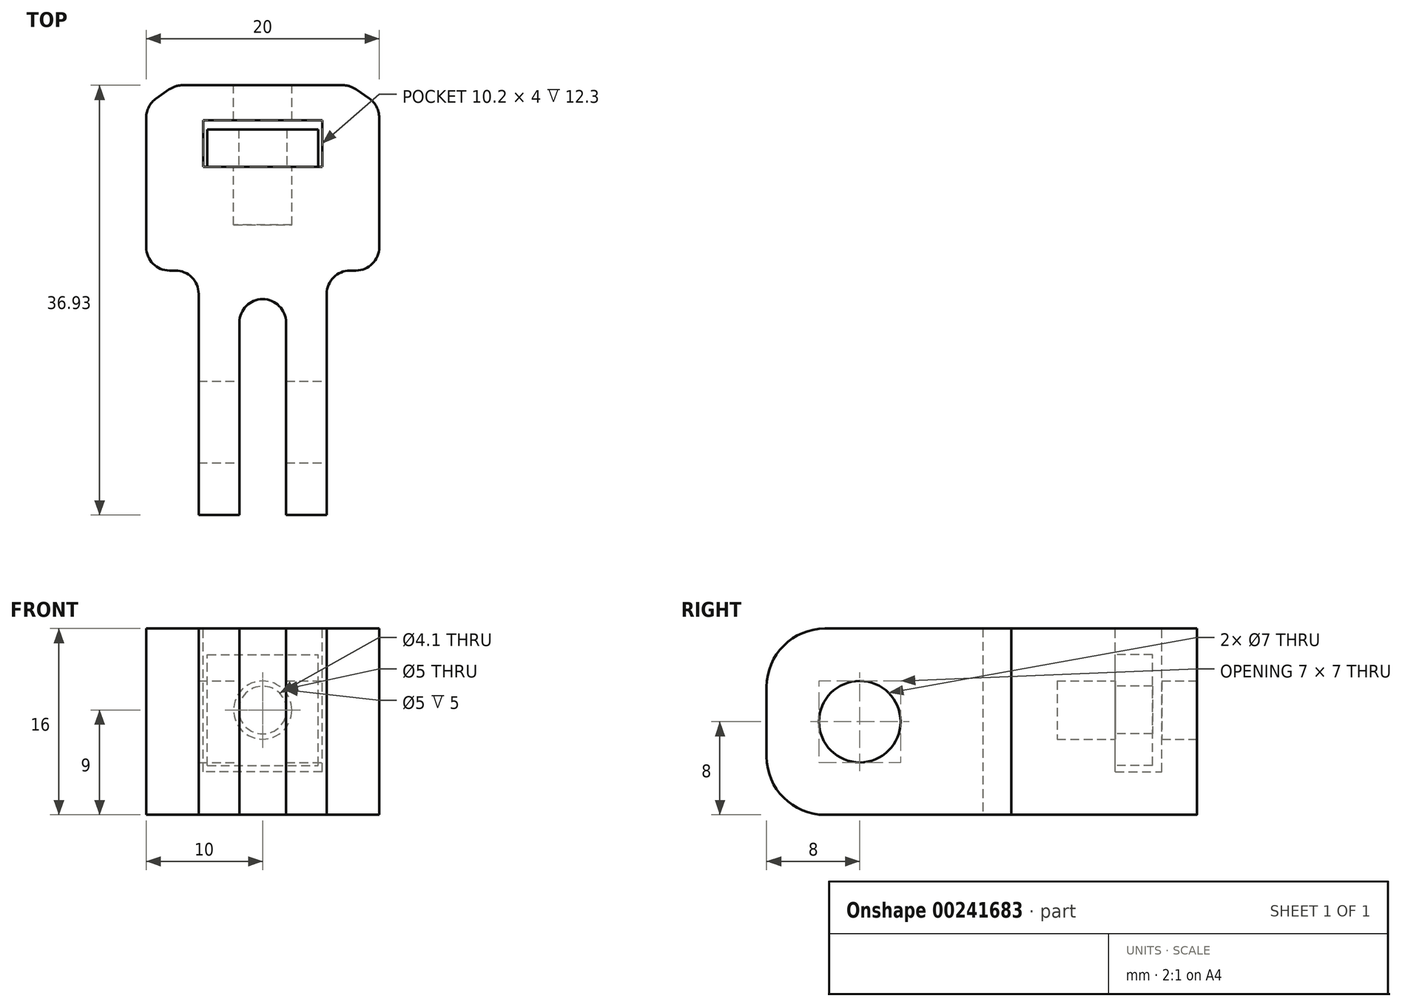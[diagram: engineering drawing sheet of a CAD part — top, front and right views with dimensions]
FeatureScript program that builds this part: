
annotation { "Feature Type Name" : "Feature", "Feature Type Description" : "" }
export const myFeature = defineFeature(function(context is Context, id is Id, definition is map)
    precondition{}
    {
        {
            var Q0;
            Q0=qCreatedBy(makeId("Top.planeOp"),FACE);
            var sketch = newSketch(context, id + "F0", { "sketchPlane" : qUnion([Q0])});
            skLineSegment(sketch, "E0.top", {"start": v(-5.5, -26) * mm, "end": v(-2, -26) * mm});
            skLineSegment(sketch, "E0.left", {"start": v(-5.5, -4.99) * mm, "end": v(-5.5, -26) * mm});
            skLineSegment(sketch, "E0.right", {"start": v(5.5, -4.99) * mm, "end": v(5.5, -26) * mm});
            skLineSegment(sketch, "E1.top", {"start": v(-2, -7.45) * mm, "end": v(2, -7.45) * mm});
            skLineSegment(sketch, "E1.left", {"start": v(-2, -26) * mm, "end": v(-2, -7.45) * mm});
            skLineSegment(sketch, "E1.right", {"start": v(2, -26) * mm, "end": v(2, -7.45) * mm});
            skLineSegment(sketch, "E2.trimOffspring", {"start": v(2, -26) * mm, "end": v(5.5, -26) * mm});
            skLineSegment(sketch, "E3.top", {"start": v(-7.5, 10.93) * mm, "end": v(7.5, 10.93) * mm});
            skLineSegment(sketch, "E4", {"start": v(0, 24.77) * mm, "end": v(0, -50.26) * mm, "construction": true});
            skPoint(sketch, "E4.startSnap0", {"position": v(0, 10.93) * mm});
            skPoint(sketch, "E4.endSnap0", {"position": v(0, -7.45) * mm});
            skLineSegment(sketch, "E5.top", {"start": v(-10, -4.99) * mm, "end": v(-5.5, -4.99) * mm});
            skLineSegment(sketch, "E5.left", {"start": v(-10, 9.2) * mm, "end": v(-10, -4.99) * mm});
            skLineSegment(sketch, "E5.right", {"start": v(10, 9.2) * mm, "end": v(10, -4.99) * mm});
            skPoint(sketch, "E5.middle", {"position": v(0, 3.2) * mm});
            skLineSegment(sketch, "E6.trimOffspring", {"start": v(5.5, -4.99) * mm, "end": v(10, -4.99) * mm});
            skLineSegment(sketch, "E7", {"start": v(10, 9.2) * mm, "end": v(7.5, 10.93) * mm});
            skLineSegment(sketch, "E8", {"start": v(-7.5, 10.93) * mm, "end": v(-10, 9.2) * mm});
            skSolve(sketch);
        }
        {
            var Q0;
            Q0=qSketchRegion(id+"F0",true);
            extrude(context, id + "F1", {"entities" : qUnion([Q0]), "depth" : 16 * mm});
        }
        {
            var Q0;
            Q0=makeQuery(id+"F1.opExtrude","SWEPT_FACE",FACE,{"disambiguationData":[OSD([sQuery(id+"F0.wireOp",EDGE,"E3.top")])]});
            var sketch = newSketch(context, id + "F2", { "sketchPlane" : qUnion([Q0])});
            skCircle(sketch, "E9", {"center": v(0, 9) * mm, "radius": 2.5 * mm});
            skSolve(sketch);
        }
        {
            var Q0;
            Q0=qSketchRegion(id+"F2",true);
            extrude(context, id + "F3", {"entities" : qUnion([Q0]), "operationType" : NewBodyOperationType.REMOVE, "oppositeDirection" : true, "depth" : 12 * mm});
        }
        {
            var Q0;
            Q0=makeQuery(id+"F1.opExtrude","SWEPT_FACE",FACE,{"disambiguationData":[OSD([sQuery(id+"F0.wireOp",EDGE,"E0.right"),sQuery(id+"F0.wireOp",EDGE,"E3.right")])]});
            var sketch = newSketch(context, id + "F4", { "sketchPlane" : qUnion([Q0])});
            skCircle(sketch, "E10", {"center": v(-18, 8) * mm, "radius": 3.5 * mm});
            skSolve(sketch);
        }
        {
            var Q0;
            Q0=qSketchRegion(id+"F4",true);
            var Q1;
            Q1=makeQuery(id+"F1.opExtrude","SWEPT_FACE",FACE,{"disambiguationData":[OSD([sQuery(id+"F0.wireOp",EDGE,"E0.left"),sQuery(id+"F0.wireOp",EDGE,"E3.left")])]});
            extrude(context, id + "F5", {"entities" : qUnion([Q0]), "operationType" : NewBodyOperationType.REMOVE, "endBound" : BoundingType.UP_TO_SURFACE, "oppositeDirection" : true, "endBoundEntityFace" : qUnion([Q1]), "depth" : 25 * mm});
        }
        {
            var Q0;
            Q0=makeQuery(id+"F1.opExtrude","SWEPT_EDGE",EDGE,{"disambiguationData":[OSD([sQuery(id+"F0.wireOp",EDGE,"E0.left"),sQuery(id+"F0.wireOp",EDGE,"E5.top")])]});
            var Q1;
            Q1=makeQuery(id+"F1.opExtrude","SWEPT_EDGE",EDGE,{"disambiguationData":[OSD([sQuery(id+"F0.wireOp",EDGE,"E1.top"),sQuery(id+"F0.wireOp",EDGE,"E1.right")])]});
            var Q2;
            Q2=makeQuery(id+"F1.opExtrude","SWEPT_EDGE",EDGE,{"disambiguationData":[OSD([sQuery(id+"F0.wireOp",EDGE,"E1.top"),sQuery(id+"F0.wireOp",EDGE,"E1.left")])]});
            var Q3;
            Q3=makeQuery(id+"F1.opExtrude","SWEPT_EDGE",EDGE,{"disambiguationData":[OSD([sQuery(id+"F0.wireOp",EDGE,"E0.right"),sQuery(id+"F0.wireOp",EDGE,"E6.trimOffspring")])]});
            fillet(context, id + "F6", {"entities" : qUnion([Q0, Q1, Q2, Q3]), "radius" : 2 * mm, "tangentPropagation" : true, "allowEdgeOverflow" : false});
        }
        {
            var Q0;
            Q0=makeQuery(id+"F1.opExtrude","CAP_FACE",FACE,{"disambiguationData":[OSD([sQuery(id+"F0.wireOp",EDGE,"E0.top"),sQuery(id+"F0.wireOp",EDGE,"E0.left"),sQuery(id+"F0.wireOp",EDGE,"E0.right"),sQuery(id+"F0.wireOp",EDGE,"E1.top"),sQuery(id+"F0.wireOp",EDGE,"E1.left"),sQuery(id+"F0.wireOp",EDGE,"E1.right"),sQuery(id+"F0.wireOp",EDGE,"E2.trimOffspring"),sQuery(id+"F0.wireOp",EDGE,"E3.top"),sQuery(id+"F0.wireOp",EDGE,"E3.left"),sQuery(id+"F0.wireOp",EDGE,"E3.right")])],"isStart":false});
            var sketch = newSketch(context, id + "F7", { "sketchPlane" : qUnion([Q0])});
            skLineSegment(sketch, "E11.bottom", {"start": v(5.1, 3.93) * mm, "end": v(-5.1, 3.93) * mm});
            skLineSegment(sketch, "E11.top", {"start": v(5.1, 7.93) * mm, "end": v(-5.1, 7.93) * mm});
            skLineSegment(sketch, "E11.left", {"start": v(5.1, 3.93) * mm, "end": v(5.1, 7.93) * mm});
            skLineSegment(sketch, "E11.right", {"start": v(-5.1, 3.93) * mm, "end": v(-5.1, 7.93) * mm});
            skPoint(sketch, "E11.middle", {"position": v(0, 5.93) * mm});
            skSolve(sketch);
        }
        {
            var Q0;
            Q0=qSketchRegion(id+"F7",true);
            extrude(context, id + "F8", {"entities" : qUnion([Q0]), "operationType" : NewBodyOperationType.REMOVE, "oppositeDirection" : true, "depth" : 12.3 * mm});
        }
        {
            var Q0;
            Q0=makeQuery(id+"F1.opExtrude","CAP_EDGE",EDGE,{"disambiguationData":[OSD([sQuery(id+"F0.wireOp",EDGE,"E2.trimOffspring")])],"isStart":false});
            var Q1;
            Q1=makeQuery(id+"F1.opExtrude","CAP_EDGE",EDGE,{"disambiguationData":[OSD([sQuery(id+"F0.wireOp",EDGE,"E2.trimOffspring")])],"isStart":true});
            var Q2;
            Q2=makeQuery(id+"F1.opExtrude","CAP_EDGE",EDGE,{"disambiguationData":[OSD([sQuery(id+"F0.wireOp",EDGE,"E0.top")])],"isStart":false});
            var Q3;
            Q3=makeQuery(id+"F1.opExtrude","CAP_EDGE",EDGE,{"disambiguationData":[OSD([sQuery(id+"F0.wireOp",EDGE,"E0.top")])],"isStart":true});
            fillet(context, id + "F9", {"entities" : qUnion([Q0, Q1, Q2, Q3]), "radius" : 5 * mm, "tangentPropagation" : true, "allowEdgeOverflow" : false});
        }
        {
            var Q0;
            Q0=makeQuery(id+"F8.boolean.opBoolean","COPY",FACE,{"derivedFrom":makeQuery(id+"F8.opExtrude","SWEPT_FACE",FACE,{"disambiguationData":[OSD([sQuery(id+"F7.wireOp",EDGE,"E11.bottom")])]})});
            var sketch = newSketch(context, id + "F10", { "sketchPlane" : qUnion([Q0])});
            skLineSegment(sketch, "E12.bottom", {"start": v(4.75, 4.25) * mm, "end": v(-4.75, 4.25) * mm});
            skLineSegment(sketch, "E12.top", {"start": v(4.75, 13.75) * mm, "end": v(-4.75, 13.75) * mm});
            skLineSegment(sketch, "E12.left", {"start": v(4.75, 4.25) * mm, "end": v(4.75, 13.75) * mm});
            skLineSegment(sketch, "E12.right", {"start": v(-4.75, 4.25) * mm, "end": v(-4.75, 13.75) * mm});
            skPoint(sketch, "E12.middle", {"position": v(0, 9) * mm});
            skCircle(sketch, "E13", {"center": v(0, 9) * mm, "radius": 2.05 * mm});
            skSolve(sketch);
        }
        {
            var Q0;
            Q0 = qSketchRegion(id + "F10", true);
            extrude(context, id + "F11", {"entities" : qUnion([Q0]), "depth" : 3.2 * mm});
        }
        {
            var Q0;
            Q0=makeQuery(id+"F1.opExtrude","SWEPT_EDGE",EDGE,{"disambiguationData":[OSD([sQuery(id+"F0.wireOp",EDGE,"E5.top"),sQuery(id+"F0.wireOp",EDGE,"E5.left")])]});
            var Q1;
            Q1=makeQuery(id+"F1.opExtrude","SWEPT_EDGE",EDGE,{"disambiguationData":[OSD([sQuery(id+"F0.wireOp",EDGE,"E5.right"),sQuery(id+"F0.wireOp",EDGE,"E6.trimOffspring")])]});
            var Q2;
            Q2=makeQuery(id+"F1.opExtrude","SWEPT_EDGE",EDGE,{"disambiguationData":[OSD([sQuery(id+"F0.wireOp",EDGE,"E5.left"),sQuery(id+"F0.wireOp",EDGE,"E8")])]});
            var Q3;
            Q3=makeQuery(id+"F1.opExtrude","SWEPT_EDGE",EDGE,{"disambiguationData":[OSD([sQuery(id+"F0.wireOp",EDGE,"E3.top"),sQuery(id+"F0.wireOp",EDGE,"E8")])]});
            var Q4;
            Q4=makeQuery(id+"F1.opExtrude","SWEPT_EDGE",EDGE,{"disambiguationData":[OSD([sQuery(id+"F0.wireOp",EDGE,"E3.top"),sQuery(id+"F0.wireOp",EDGE,"E7")])]});
            var Q5;
            Q5=makeQuery(id+"F1.opExtrude","SWEPT_EDGE",EDGE,{"disambiguationData":[OSD([sQuery(id+"F0.wireOp",EDGE,"E5.right"),sQuery(id+"F0.wireOp",EDGE,"E7")])]});
            fillet(context, id + "F12", {"entities" : qUnion([Q0, Q1, Q2, Q3, Q4, Q5]), "radius" : 2 * mm, "tangentPropagation" : true, "allowEdgeOverflow" : false});
        }
    });
